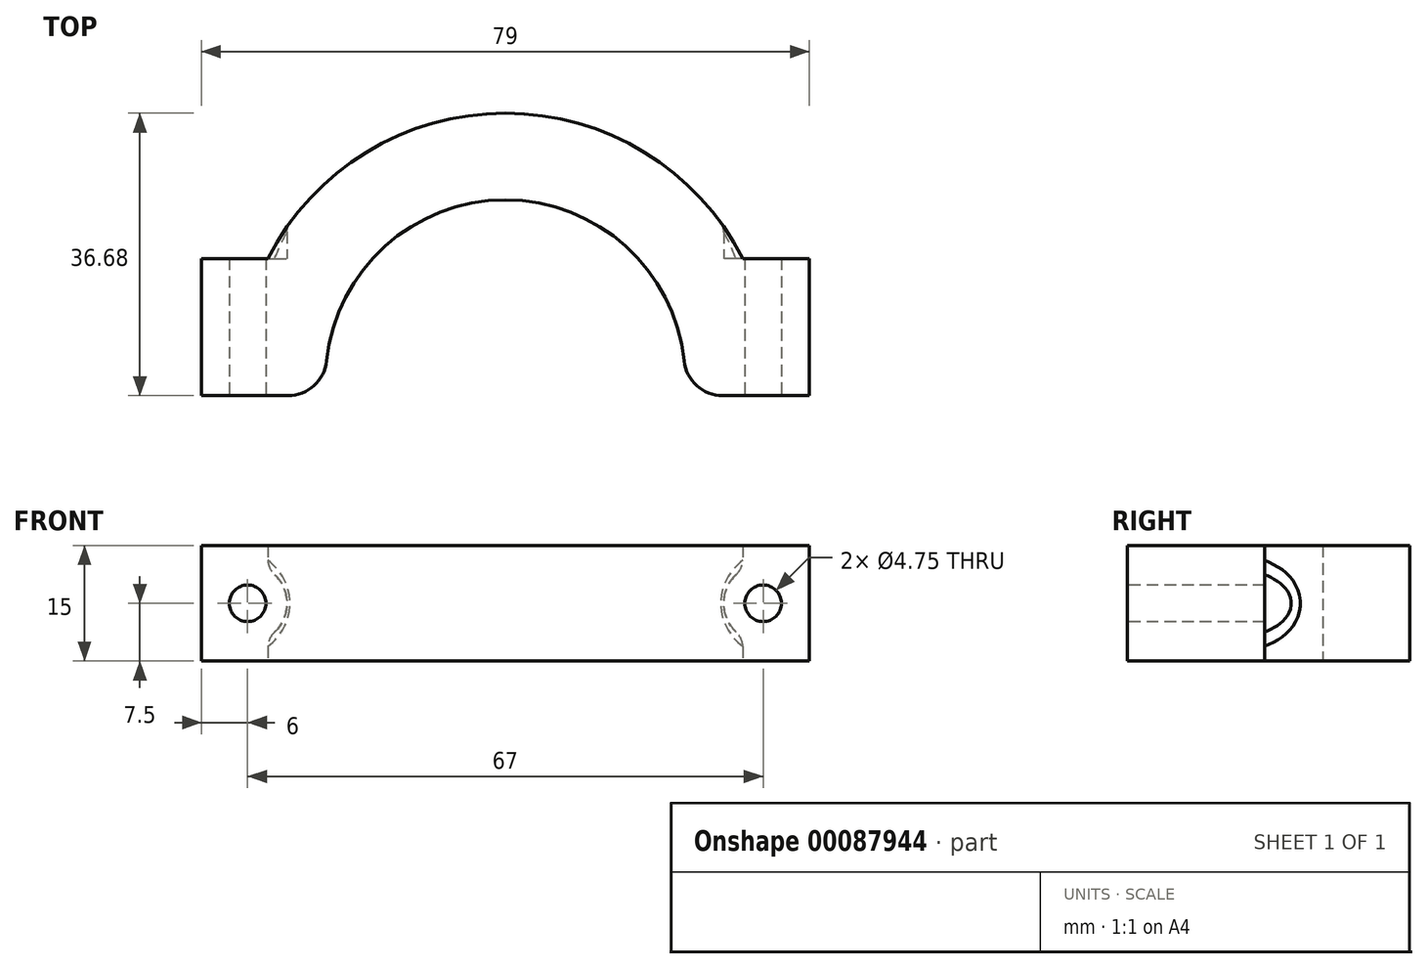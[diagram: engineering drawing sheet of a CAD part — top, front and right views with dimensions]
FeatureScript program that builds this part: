
annotation { "Feature Type Name" : "Feature", "Feature Type Description" : "" }
export const myFeature = defineFeature(function(context is Context, id is Id, definition is map)
    precondition{}
    {
        {
            var Q0;
            Q0=qCreatedBy(makeId("Top.planeOp"),FACE);
            var sketch = newSketch(context, id + "F0", { "sketchPlane" : qUnion([Q0])});
            skLineSegment(sketch, "E0", {"start": v(12.94, 0) * mm, "end": v(17.04, 0) * mm, "construction": true});
            skArc(sketch, "E1", {"start": v(12.94, 0) * mm, "mid": v(6.76, 2.9) * mm, "end": v(0, 3.9) * mm});
            skArc(sketch, "E2", {"start": v(25.4, -15.34) * mm, "mid": v(22.6, -6.92) * mm, "end": v(17.04, 0) * mm, "construction": true});
            skLineSegment(sketch, "E3", {"start": v(25.4, -15.34) * mm, "end": v(27.2, -21.5) * mm, "construction": true});
            skLineSegment(sketch, "E4", {"start": v(28.22, -21.5) * mm, "end": v(39.5, -21.5) * mm});
            skLineSegment(sketch, "E5", {"start": v(39.5, -21.5) * mm, "end": v(39.5, -3.7) * mm});
            skLineSegment(sketch, "E6", {"start": v(39.5, -3.7) * mm, "end": v(30.85, -3.7) * mm});
            skArc(sketch, "E7", {"start": v(30.85, -3.7) * mm, "mid": v(18.08, 10.09) * mm, "end": v(0, 15.18) * mm});
            skLineSegment(sketch, "E8", {"start": v(0, 3.9) * mm, "end": v(0, 15.18) * mm, "construction": true});
            skPoint(sketch, "E9.orphan", {"position": v(-12.94, 0) * mm});
            skLineSegment(sketch, "E10.MirrorCS", {"start": v(-25.4, -15.34) * mm, "end": v(-27.2, -21.5) * mm, "construction": true});
            skLineSegment(sketch, "E11.MirrorCS", {"start": v(-12.94, 0) * mm, "end": v(-17.04, 0) * mm, "construction": true});
            skLineSegment(sketch, "E12.MirrorCS", {"start": v(-28.22, -21.5) * mm, "end": v(-39.5, -21.5) * mm});
            skArc(sketch, "E13.MirrorCS", {"start": v(-30.85, -3.7) * mm, "mid": v(-18.08, 10.09) * mm, "end": v(0, 15.18) * mm});
            skLineSegment(sketch, "E14.MirrorCS", {"start": v(-39.5, -3.7) * mm, "end": v(-30.85, -3.7) * mm});
            skLineSegment(sketch, "E15.MirrorCS", {"start": v(-39.5, -21.5) * mm, "end": v(-39.5, -3.7) * mm});
            skArc(sketch, "E16.MirrorCS", {"start": v(-25.4, -15.34) * mm, "mid": v(-22.6, -6.92) * mm, "end": v(-17.04, 0) * mm, "construction": true});
            skArc(sketch, "E17.MirrorCS", {"start": v(-12.94, 0) * mm, "mid": v(-6.76, 2.9) * mm, "end": v(0, 3.9) * mm});
            skPoint(sketch, "E18.MirrorP", {"position": v(12.94, 0) * mm});
            skArc(sketch, "E19", {"start": v(-12.94, 0) * mm, "mid": v(-20, -7.36) * mm, "end": v(-23.25, -17.02) * mm});
            skArc(sketch, "E20", {"start": v(23.25, -17.02) * mm, "mid": v(20, -7.36) * mm, "end": v(12.94, 0) * mm});
            skPoint(sketch, "E21.visualSharp", {"position": v(-23.29, -21.5) * mm});
            skArc(sketch, "E21.filletArc", {"start": v(-28.22, -21.5) * mm, "mid": v(-24.87, -20.21) * mm, "end": v(-23.25, -17.02) * mm});
            skPoint(sketch, "E22.visualSharp", {"position": v(23.29, -21.5) * mm});
            skArc(sketch, "E22.filletArc", {"start": v(23.25, -17.02) * mm, "mid": v(24.87, -20.21) * mm, "end": v(28.22, -21.5) * mm});
            skSolve(sketch);
        }
        {
            var Q0;
            Q0 = qSketchRegion(id + "F0", true);
            extrude(context, id + "F1", {"entities" : qUnion([Q0]), "depth" : 15 * mm});
        }
        {
            var Q0;
            Q0=makeQuery(id+"F1.opExtrude","SWEPT_FACE",FACE,{"disambiguationData":[OSD([sQuery(id+"F0.wireOp",EDGE,"E12.MirrorCS")])]});
            var sketch = newSketch(context, id + "F2", { "sketchPlane" : qUnion([Q0])});
            skLineSegment(sketch, "E23", {"start": v(-31.13, 7.5) * mm, "end": v(31.13, 7.5) * mm, "construction": true});
            skCircle(sketch, "E24", {"center": v(-33.5, 7.5) * mm, "radius": 2.38 * mm});
            skCircle(sketch, "E25", {"center": v(33.5, 7.5) * mm, "radius": 2.38 * mm});
            skLineSegment(sketch, "E26", {"start": v(0, 0) * mm, "end": v(0, 7.5) * mm, "construction": true});
            skLineSegment(sketch, "E27", {"start": v(33.5, 7.5) * mm, "end": v(39.5, 7.5) * mm, "construction": true});
            skSolve(sketch);
        }
        {
            var Q0;
            Q0=makeQuery(id+"F2.imprint","IMPRINT",FACE,{"disambiguationData":[TD([[makeQuery(id+"F2.imprint","IMPRINT",EDGE,{"derivedFrom":sQuery(id+"F2.wireOp",EDGE,"E24")}),1.0]])]});
            var Q1;
            Q1=makeQuery(id+"F2.imprint","IMPRINT",FACE,{"disambiguationData":[TD([[makeQuery(id+"F2.imprint","IMPRINT",EDGE,{"derivedFrom":sQuery(id+"F2.wireOp",EDGE,"E25")}),1.0]])]});
            extrude(context, id + "F3", {"entities" : qUnion([Q0, Q1]), "operationType" : NewBodyOperationType.REMOVE, "oppositeDirection" : true, "depth" : 25 * mm});
        }
        {
            var Q0;
            Q0=makeQuery(id+"F1.opExtrude","SWEPT_FACE",FACE,{"disambiguationData":[OSD([sQuery(id+"F0.wireOp",EDGE,"E14.MirrorCS")])]});
            var sketch = newSketch(context, id + "F4", { "sketchPlane" : qUnion([Q0])});
            skCircle(sketch, "E28", {"center": v(33.5, 7.5) * mm, "radius": 5.12 * mm});
            skCircle(sketch, "E29", {"center": v(-33.5, 7.5) * mm, "radius": 5.12 * mm});
            skSolve(sketch);
        }
        {
            var Q0;
            Q0=qSketchRegion(id+"F4",true);
            extrude(context, id + "F5", {"entities" : qUnion([Q0]), "operationType" : NewBodyOperationType.REMOVE, "depth" : 25 * mm});
        }
        {
            var Q0;
            Q0=makeQuery(id+"F5.boolean.opBoolean","INTERSECT",EDGE,{"derivedFrom":[makeQuery(id+"F1.opExtrude","SWEPT_FACE",FACE,{"disambiguationData":[OSD([sQuery(id+"F0.wireOp",EDGE,"E7"),sQuery(id+"F0.wireOp",EDGE,"E13.MirrorCS")])]}),makeQuery(id+"F5.opExtrude","SWEPT_FACE",FACE,{"disambiguationData":[OSD([sQuery(id+"F4.wireOp",EDGE,"E29")])]})]});
            var Q1;
            Q1=makeQuery(id+"F5.boolean.opBoolean","INTERSECT",EDGE,{"derivedFrom":[makeQuery(id+"F1.opExtrude","SWEPT_FACE",FACE,{"disambiguationData":[OSD([sQuery(id+"F0.wireOp",EDGE,"E7"),sQuery(id+"F0.wireOp",EDGE,"E13.MirrorCS")])]}),makeQuery(id+"F5.opExtrude","SWEPT_FACE",FACE,{"disambiguationData":[OSD([sQuery(id+"F4.wireOp",EDGE,"E28")])]})]});
            fillet(context, id + "F6", {"entities" : qUnion([Q0, Q1]), "radius" : 2 * mm, "tangentPropagation" : true, "allowEdgeOverflow" : false});
        }
    });
